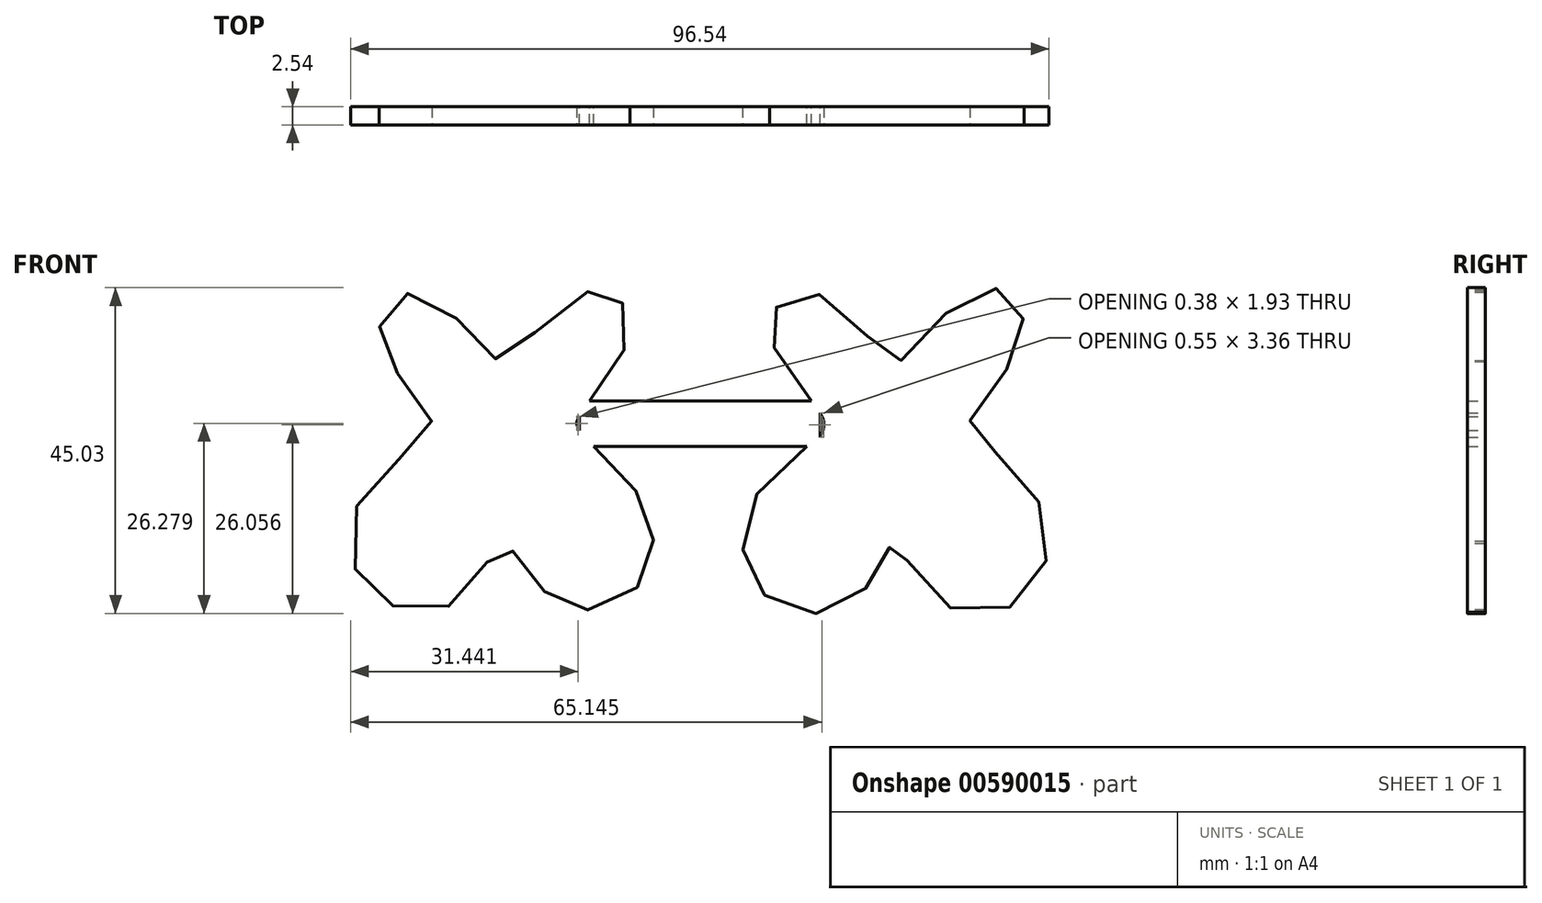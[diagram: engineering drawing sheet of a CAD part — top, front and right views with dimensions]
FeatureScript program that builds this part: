
annotation { "Feature Type Name" : "Feature", "Feature Type Description" : "" }
export const myFeature = defineFeature(function(context is Context, id is Id, definition is map)
    precondition{}
    {
        {
            var Q0;
            Q0=qCreatedBy(makeId("Front.planeOp"),FACE);
            var sketch = newSketch(context, id + "F0", { "sketchPlane" : qUnion([Q0])});
            skFitSpline(sketch, "E0", {"points": [v(-118.49, -19.97) * mm, v(-113.1, -15.54) * mm, v(-111.7, -13.8) * mm, v(-111.98, -12.04) * mm, v(-114.7, -8.41) * mm, v(-117.9, -4.03) * mm, v(-118.93, -1.41) * mm, v(-118.67, 1.36) * mm, v(-117.63, 3.33) * mm, v(-114.75, 4.89) * mm, v(-112.1, 4.35) * mm, v(-107.5, 0.66) * mm, v(-104.28, -2.73) * mm, v(-102.53, -4.46) * mm, v(-100.96, -4.4) * mm, v(-97.42, -0.58) * mm, v(-91.95, 4.05) * mm, v(-89.25, 5.3) * mm, v(-87.38, 5.15) * mm, v(-85.8, 4.1) * mm, v(-84.47, 1.84) * mm, v(-84.46, -0.93) * mm, v(-86.25, -5.28) * mm, v(-89.18, -9.16) * mm, v(-91.34, -12.3) * mm, v(-91.64, -13.28) * mm, v(-90.42, -15.23) * mm, v(-87.94, -17.64) * mm, v(-84.18, -21.56) * mm, v(-81.94, -25.02) * mm, v(-81.03, -28.39) * mm, v(-81.46, -31.76) * mm, v(-82.64, -34.82) * mm, v(-84.9, -37.48) * mm, v(-89.07, -38.96) * mm, v(-92.73, -38.47) * mm, v(-95.07, -37.28) * mm, v(-97.29, -35.23) * mm, v(-99.51, -32.16) * mm, v(-101.1, -30.03) * mm, v(-101.86, -29.48) * mm, v(-103.24, -31.04) * mm, v(-105.69, -35.04) * mm, v(-108.83, -38.17) * mm, v(-112.49, -39.1) * mm, v(-116.91, -38.45) * mm, v(-120.08, -36.55) * mm, v(-122.24, -33.4) * mm, v(-122.83, -27.82) * mm, v(-121.52, -23.5) * mm, v(-118.49, -19.97) * mm]});
            skFitSpline(sketch, "E1", {"points": [v(-66, -21.88) * mm, v(-60.64, -16.83) * mm, v(-58.03, -15.05) * mm, v(-57.5, -12.93) * mm, v(-58.37, -11.2) * mm, v(-60.68, -8.18) * mm, v(-64.38, -2.61) * mm, v(-64.98, 0) * mm, v(-64.34, 2.37) * mm, v(-62.58, 4.4) * mm, v(-59.1, 5.04) * mm, v(-54.62, 2) * mm, v(-50.53, -2.1) * mm, v(-48.42, -4.15) * mm, v(-46.85, -4.48) * mm, v(-44.37, -1.8) * mm, v(-37.83, 4.3) * mm, v(-34.49, 5.6) * mm, v(-32.25, 4.93) * mm, v(-30.54, 3.13) * mm, v(-29.8, 0) * mm, v(-30.5, -2.91) * mm, v(-35.47, -10.08) * mm, v(-37.3, -12.77) * mm, v(-36.83, -14.4) * mm, v(-35.38, -15.71) * mm, v(-30.96, -19.97) * mm, v(-27.46, -24.65) * mm, v(-26.38, -30.12) * mm, v(-27.8, -34.44) * mm, v(-31.47, -38.43) * mm, v(-36.78, -39.22) * mm, v(-41.31, -37.98) * mm, v(-45.74, -32.57) * mm, v(-46.8, -30.7) * mm, v(-47.39, -29.95) * mm, v(-47.94, -29.85) * mm, v(-48.5, -30.49) * mm, v(-49.77, -32.99) * mm, v(-51.97, -36.33) * mm, v(-55.59, -39) * mm, v(-60.83, -39.22) * mm, v(-64.64, -37.76) * mm, v(-67.6, -34.57) * mm, v(-68.61, -31.25) * mm, v(-68.4, -26.84) * mm, v(-66, -21.88) * mm]});
            skLineSegment(sketch, "E2.bottom", {"start": v(-91.27, -10.07) * mm, "end": v(-58.03, -10.07) * mm});
            skLineSegment(sketch, "E2.top", {"start": v(-91.27, -16.37) * mm, "end": v(-58.03, -16.37) * mm});
            skLineSegment(sketch, "E2.left", {"start": v(-91.27, -10.07) * mm, "end": v(-91.27, -16.37) * mm});
            skLineSegment(sketch, "E2.right", {"start": v(-58.03, -10.07) * mm, "end": v(-58.03, -16.37) * mm});
            skPoint(sketch, "E3", {"position": v(-63, 0) * mm});
            skPoint(sketch, "E4", {"position": v(-59.1, 0) * mm});
            skPoint(sketch, "E5", {"position": v(-55, 0) * mm});
            skPoint(sketch, "E6", {"position": v(-39.8, 0) * mm});
            skPoint(sketch, "E7", {"position": v(-35.56, 0) * mm});
            skPoint(sketch, "E8", {"position": v(-31.65, 0) * mm});
            skPoint(sketch, "E9", {"position": v(-61.16, -3.79) * mm});
            skPoint(sketch, "E10", {"position": v(-57.87, -3.79) * mm});
            skPoint(sketch, "E11", {"position": v(-53.64, -3.79) * mm});
            skPoint(sketch, "E12", {"position": v(-41.26, -3.79) * mm});
            skPoint(sketch, "E13", {"position": v(-37.19, -3.79) * mm});
            skPoint(sketch, "E14", {"position": v(-33.43, -3.79) * mm});
            skPoint(sketch, "E15", {"position": v(-57.92, -7.56) * mm});
            skPoint(sketch, "E16", {"position": v(-53.06, -7.64) * mm});
            skPoint(sketch, "E17", {"position": v(-48.2, -7.64) * mm});
            skPoint(sketch, "E18", {"position": v(-43.04, -7.64) * mm});
            skPoint(sketch, "E19", {"position": v(-37.19, -7.64) * mm});
            skPoint(sketch, "E20", {"position": v(-55, -12.93) * mm});
            skPoint(sketch, "E21", {"position": v(-50.53, -12.93) * mm});
            skPoint(sketch, "E22", {"position": v(-45.15, -12.93) * mm});
            skPoint(sketch, "E23", {"position": v(-39.8, -12.93) * mm});
            skPoint(sketch, "E24", {"position": v(-57.5, -18.01) * mm});
            skPoint(sketch, "E25", {"position": v(-50.53, -18.1) * mm});
            skPoint(sketch, "E26", {"position": v(-45.15, -18.1) * mm});
            skPoint(sketch, "E27", {"position": v(-39.8, -18.1) * mm});
            skPoint(sketch, "E28", {"position": v(-54.14, -17.9) * mm});
            skPoint(sketch, "E29", {"position": v(-35.34, -18.1) * mm});
            skPoint(sketch, "E30", {"position": v(-62.34, -21.51) * mm});
            skPoint(sketch, "E31", {"position": v(-57.95, -21.28) * mm});
            skPoint(sketch, "E32", {"position": v(-54.14, -21.5) * mm});
            skPoint(sketch, "E33", {"position": v(-49.8, -21.4) * mm});
            skPoint(sketch, "E34", {"position": v(-45.15, -21.32) * mm});
            skPoint(sketch, "E35", {"position": v(-39.8, -21.32) * mm});
            skPoint(sketch, "E36", {"position": v(-34.13, -21.32) * mm});
            skPoint(sketch, "E37", {"position": v(-64.43, -25.2) * mm});
            skPoint(sketch, "E38", {"position": v(-60.5, -25.12) * mm});
            skPoint(sketch, "E39", {"position": v(-55.5, -25.04) * mm});
            skPoint(sketch, "E40", {"position": v(-51.26, -25.04) * mm});
            skPoint(sketch, "E41", {"position": v(-45.15, -25.04) * mm});
            skPoint(sketch, "E42", {"position": v(-39.8, -25.04) * mm});
            skPoint(sketch, "E43", {"position": v(-33.56, -25.04) * mm});
            skPoint(sketch, "E44", {"position": v(-31.72, -28.38) * mm});
            skPoint(sketch, "E45", {"position": v(-35.34, -28.38) * mm});
            skPoint(sketch, "E46", {"position": v(-39.8, -28.38) * mm});
            skPoint(sketch, "E47", {"position": v(-45.15, -28.38) * mm});
            skPoint(sketch, "E48", {"position": v(-51.26, -28.38) * mm});
            skPoint(sketch, "E49", {"position": v(-55.5, -28.38) * mm});
            skPoint(sketch, "E50", {"position": v(-61.34, -28.38) * mm});
            skPoint(sketch, "E51", {"position": v(-64.47, -28.38) * mm});
            skPoint(sketch, "E52", {"position": v(-64.47, -31.9) * mm});
            skPoint(sketch, "E53", {"position": v(-59.97, -31.9) * mm});
            skPoint(sketch, "E54", {"position": v(-54.14, -31.9) * mm});
            skPoint(sketch, "E55", {"position": v(-61.34, -35.83) * mm});
            skPoint(sketch, "E56", {"position": v(-55.5, -35.9) * mm});
            skPoint(sketch, "E57", {"position": v(-39.8, -34.57) * mm});
            skPoint(sketch, "E58", {"position": v(-33.56, -34.57) * mm});
            skPoint(sketch, "E59", {"position": v(-41.63, -31.9) * mm});
            skPoint(sketch, "E60", {"position": v(-35.34, -31.9) * mm});
            skPoint(sketch, "E61", {"position": v(-31.72, -31.9) * mm});
            skPoint(sketch, "E62", {"position": v(-128.72, -21.32) * mm});
            skPoint(sketch, "E63", {"position": v(-116.92, 0.66) * mm});
            skPoint(sketch, "E64", {"position": v(-114.22, 0.66) * mm});
            skPoint(sketch, "E65", {"position": v(-110.94, 0.66) * mm});
            skPoint(sketch, "E66", {"position": v(-93.96, 0) * mm});
            skPoint(sketch, "E67", {"position": v(-90.78, 0) * mm});
            skPoint(sketch, "E68", {"position": v(-87.4, 0) * mm});
            skPoint(sketch, "E69", {"position": v(-116.92, -2.22) * mm});
            skPoint(sketch, "E70", {"position": v(-114.22, -2.27) * mm});
            skPoint(sketch, "E71", {"position": v(-110.5, -2.23) * mm});
            skPoint(sketch, "E72", {"position": v(-107.12, -1.9) * mm});
            skPoint(sketch, "E73", {"position": v(-96.41, -2.07) * mm});
            skPoint(sketch, "E74", {"position": v(-93.13, -2.4) * mm});
            skPoint(sketch, "E75", {"position": v(-89.95, -2.4) * mm});
            skPoint(sketch, "E76", {"position": v(-87.4, -2.4) * mm});
            skPoint(sketch, "E77", {"position": v(-115.37, -5.55) * mm});
            skPoint(sketch, "E78", {"position": v(-112.1, -5.6) * mm});
            skPoint(sketch, "E79", {"position": v(-108.13, -5.6) * mm});
            skPoint(sketch, "E80", {"position": v(-104.66, -5.6) * mm});
            skPoint(sketch, "E81", {"position": v(-98.38, -4.8) * mm});
            skPoint(sketch, "E82", {"position": v(-93.96, -5.6) * mm});
            skPoint(sketch, "E83", {"position": v(-89.9, -5.6) * mm});
            skPoint(sketch, "E84", {"position": v(-112.1, -9.1) * mm});
            skPoint(sketch, "E85", {"position": v(-107.7, -9.15) * mm});
            skPoint(sketch, "E86", {"position": v(-103.46, -9.15) * mm});
            skPoint(sketch, "E87", {"position": v(-99.59, -9.15) * mm});
            skPoint(sketch, "E88", {"position": v(-93.96, -9.15) * mm});
            skPoint(sketch, "E89", {"position": v(-109.68, -12.7) * mm});
            skPoint(sketch, "E90", {"position": v(-106.78, -12.84) * mm});
            skPoint(sketch, "E91", {"position": v(-103.4, -12.7) * mm});
            skPoint(sketch, "E92", {"position": v(-99.74, -12.76) * mm});
            skPoint(sketch, "E93", {"position": v(-93.13, -12.76) * mm});
            skPoint(sketch, "E94", {"position": v(-111.38, -17.36) * mm});
            skPoint(sketch, "E95", {"position": v(-107.7, -17.52) * mm});
            skPoint(sketch, "E96", {"position": v(-101.93, -17.5) * mm});
            skPoint(sketch, "E97", {"position": v(-96.81, -17.5) * mm});
            skPoint(sketch, "E98", {"position": v(-93.13, -17.5) * mm});
            skPoint(sketch, "E99", {"position": v(-105.2, -17.5) * mm});
            skPoint(sketch, "E100", {"position": v(-115.88, -21.52) * mm});
            skPoint(sketch, "E101", {"position": v(-110.86, -21.5) * mm});
            skPoint(sketch, "E102", {"position": v(-107.7, -21.5) * mm});
            skPoint(sketch, "E103", {"position": v(-102.75, -21.5) * mm});
            skPoint(sketch, "E104", {"position": v(-97.83, -21.51) * mm});
            skPoint(sketch, "E105", {"position": v(-93.2, -21.86) * mm});
            skPoint(sketch, "E106", {"position": v(-96.84, -12.53) * mm});
            skPoint(sketch, "E107", {"position": v(-96.84, -7.85) * mm});
            skPoint(sketch, "E108", {"position": v(-101.93, -6.58) * mm});
            skPoint(sketch, "E109", {"position": v(-87.4, -21.5) * mm});
            skPoint(sketch, "E110", {"position": v(-118.34, -25.52) * mm});
            skPoint(sketch, "E111", {"position": v(-112.1, -25.8) * mm});
            skPoint(sketch, "E112", {"position": v(-104.83, -25.54) * mm});
            skPoint(sketch, "E113", {"position": v(-96.84, -25.84) * mm});
            skPoint(sketch, "E114", {"position": v(-87.94, -25.51) * mm});
            skPoint(sketch, "E115", {"position": v(-118.42, -31.21) * mm});
            skPoint(sketch, "E116", {"position": v(-112.25, -31.4) * mm});
            skPoint(sketch, "E117", {"position": v(-106.65, -31.11) * mm});
            skPoint(sketch, "E118", {"position": v(-95.84, -31.18) * mm});
            skPoint(sketch, "E119", {"position": v(-90.42, -31.17) * mm});
            skPoint(sketch, "E120", {"position": v(-85.52, -31.25) * mm});
            skPoint(sketch, "E121", {"position": v(-93.13, -35.18) * mm});
            skPoint(sketch, "E122", {"position": v(-85.67, -35.56) * mm});
            skPoint(sketch, "E123", {"position": v(-93.13, -27.84) * mm});
            skPoint(sketch, "E124", {"position": v(-116.92, -35.55) * mm});
            skPoint(sketch, "E125", {"position": v(-110.86, -35.55) * mm});
            skPoint(sketch, "E126", {"position": v(-115.78, -28.59) * mm});
            skPoint(sketch, "E127", {"position": v(-107.7, -28.52) * mm});
            skPoint(sketch, "E128", {"position": v(-99.74, -26.9) * mm});
            skPoint(sketch, "E129", {"position": v(-100.57, -24.41) * mm});
            skSolve(sketch);
        }
        {
            var Q0;
            Q0 = qSketchRegion(id + "F0", true);
            extrude(context, id + "F1", {"entities" : qUnion([Q0]), "depth" : 2.54 * mm, "offsetDistance" : 25.4 * mm});
        }
    });
